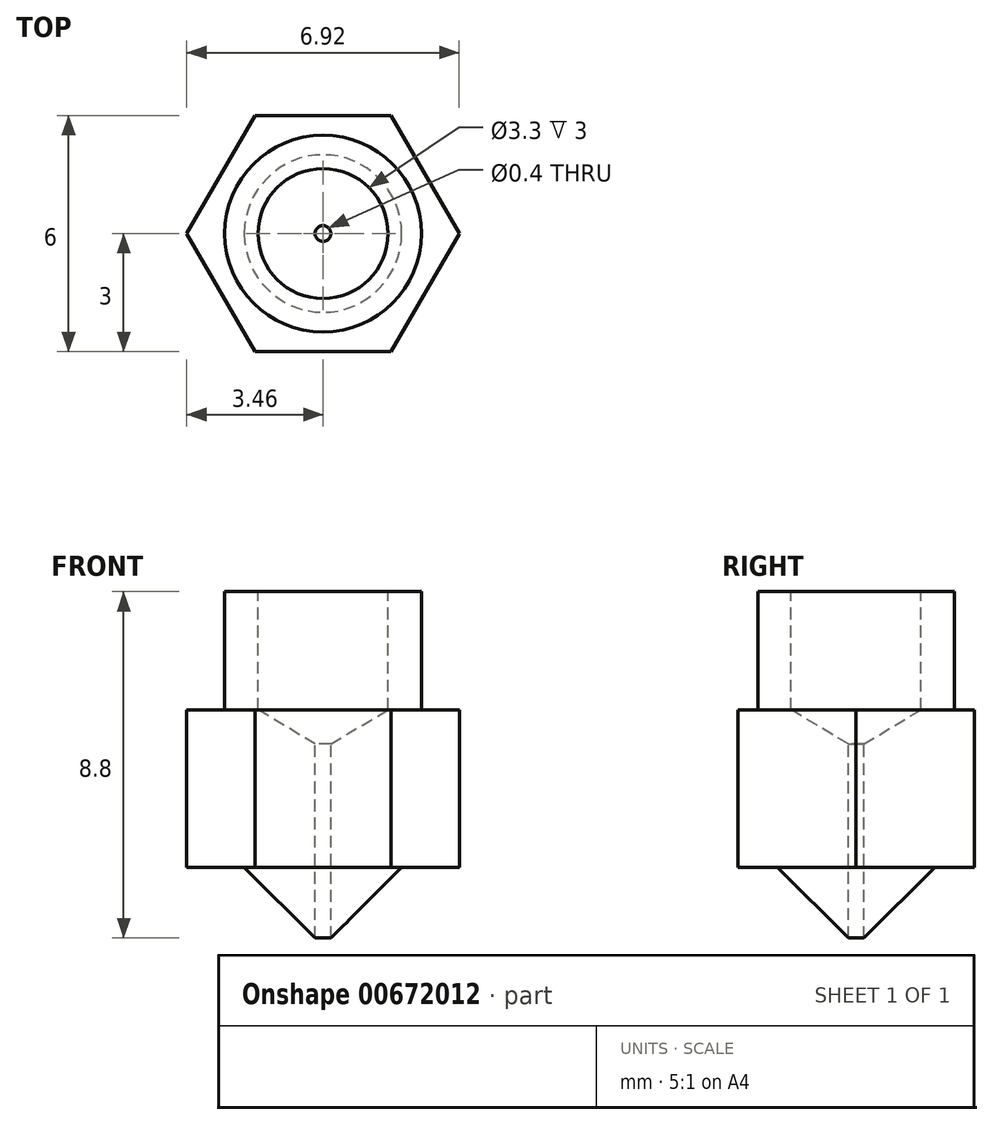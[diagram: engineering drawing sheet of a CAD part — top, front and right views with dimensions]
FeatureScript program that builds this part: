
annotation { "Feature Type Name" : "Feature", "Feature Type Description" : "" }
export const myFeature = defineFeature(function(context is Context, id is Id, definition is map)
    precondition{}
    {
        {
            var Q0;
            Q0=qCreatedBy(makeId("Front.planeOp"),FACE);
            var sketch = newSketch(context, id + "F0", { "sketchPlane" : qUnion([Q0])});
            skLineSegment(sketch, "E0", {"start": v(0, 0) * mm, "end": v(0, 3) * mm});
            skLineSegment(sketch, "E1", {"start": v(0, 3) * mm, "end": v(2.5, 3) * mm});
            skLineSegment(sketch, "E2", {"start": v(2.5, 3) * mm, "end": v(2.5, 0) * mm});
            skLineSegment(sketch, "E3", {"start": v(2.5, 0) * mm, "end": v(0, 0) * mm});
            skSolve(sketch);
        }
        {
            var Q0;
            Q0=makeQuery(id+"F0.imprint","IMPRINT",FACE,{"disambiguationData":[TD([[makeQuery(id+"F0.imprint","IMPRINT",EDGE,{"derivedFrom":sQuery(id+"F0.wireOp",EDGE,"E0")}),-1.0]])]});
            var Q1;
            Q1=sQuery(id+"F0.wireOp",EDGE,"E0");
            revolve(context, id + "F1", {"entities" : qUnion([Q0]), "axis" : qUnion([Q1]), "revolveType" : RevolveType.FULL});
        }
        {
            var Q0;
            Q0=makeQuery(id+"F1.opRevolve","SWEPT_FACE",FACE,{"disambiguationData":[OSD([sQuery(id+"F0.wireOp",EDGE,"E3")])]});
            var sketch = newSketch(context, id + "F2", { "sketchPlane" : qUnion([Q0])});
            skCircle(sketch, "E4.cCircle", {"center": v(0, 0) * mm, "radius": 3 * mm, "construction": true});
            skLineSegment(sketch, "E4.0", {"start": v(-1.73, 3) * mm, "end": v(1.73, 3) * mm});
            skLineSegment(sketch, "E4.1", {"start": v(1.73, 3) * mm, "end": v(3.46, 0) * mm});
            skLineSegment(sketch, "E4.2", {"start": v(3.46, 0) * mm, "end": v(1.73, -3) * mm});
            skLineSegment(sketch, "E4.3", {"start": v(1.73, -3) * mm, "end": v(-1.73, -3) * mm});
            skLineSegment(sketch, "E4.4", {"start": v(-1.73, -3) * mm, "end": v(-3.46, 0) * mm});
            skLineSegment(sketch, "E4.5", {"start": v(-3.46, 0) * mm, "end": v(-1.73, 3) * mm});
            skPoint(sketch, "E4.0.midPoint", {"position": v(0, 3) * mm});
            skSolve(sketch);
        }
        {
            var Q0;
            Q0=makeQuery(id+"F2.imprint","IMPRINT",FACE,{"disambiguationData":[TD([[makeQuery(id+"F2.imprint","IMPRINT",EDGE,{"derivedFrom":sQuery(id+"F2.wireOp",EDGE,"E4.0")}),-1.0]])]});
            var Q1;
            Q1=makeQuery(id+"F2.imprint","IMPRINT",FACE,{"disambiguationData":[TD([[makeQuery(id+"F2.imprint","IMPRINT",EDGE,{"derivedFrom":makeQuery(id+"F1.opRevolve","SWEPT_EDGE",EDGE,{"disambiguationData":[OSD([sQuery(id+"F0.wireOp",EDGE,"E2"),sQuery(id+"F0.wireOp",EDGE,"E3")])]})}),1.0]])]});
            extrude(context, id + "F3", {"entities" : qUnion([Q0, Q1]), "operationType" : NewBodyOperationType.ADD, "depth" : 4 * mm, "offsetDistance" : 25 * mm});
        }
        {
            var Q0;
            Q0=qCreatedBy(makeId("Front.planeOp"),FACE);
            var sketch = newSketch(context, id + "F4", { "sketchPlane" : qUnion([Q0])});
            skLineSegment(sketch, "E5", {"start": v(0, -4) * mm, "end": v(2, -4) * mm});
            skLineSegment(sketch, "E6", {"start": v(2, -4) * mm, "end": v(0, -6) * mm});
            skLineSegment(sketch, "E7", {"start": v(0, -6) * mm, "end": v(0, -4) * mm});
            skSolve(sketch);
        }
        {
            var Q0;
            Q0=makeQuery(id+"F4.imprint","IMPRINT",FACE,{"disambiguationData":[TD([[makeQuery(id+"F4.imprint","IMPRINT",EDGE,{"derivedFrom":sQuery(id+"F4.wireOp",EDGE,"E5")}),-1.0]])]});
            var Q1;
            Q1=sQuery(id+"F4.wireOp",EDGE,"E7");
            revolve(context, id + "F5", {"operationType" : NewBodyOperationType.ADD, "entities" : qUnion([Q0]), "axis" : qUnion([Q1]), "revolveType" : RevolveType.FULL});
        }
        {
            var Q0;
            Q0=makeQuery(id+"F1.opRevolve","SWEPT_FACE",FACE,{"disambiguationData":[OSD([sQuery(id+"F0.wireOp",EDGE,"E1")])]});
            var sketch = newSketch(context, id + "F6", { "sketchPlane" : qUnion([Q0])});
            skPoint(sketch, "E8", {"position": v(0, 0) * mm});
            skSolve(sketch);
        }
        {
            var Q0;
            Q0=sQuery(id+"F6.wireOp",VERTEX,"E8");
            var Q1;
            Q1=makeQuery(id+"F1.opRevolve","SWEPT_BODY",BODY,{"disambiguationData":[OSD([sQuery(id+"F0.wireOp",EDGE,"E0"),sQuery(id+"F0.wireOp",EDGE,"E1"),sQuery(id+"F0.wireOp",EDGE,"E2"),sQuery(id+"F0.wireOp",EDGE,"E3")])]});
            hole(context, id + "F7", {"style" : HoleStyle.SIMPLE, "endStyle" : HoleEndStyle.BLIND, "standardTappedOrClearance" : lookupTablePath({ "standard" : "ISO", "fit" : "Normal", "size" : "M3", "type" : "Clearance" }), "standardBlindInLast" : lookupTablePath({ "fit" : "Standard", "standard" : "ISO", "size" : "M3", "type" : "Clearance" }), "holeDiameter" : 3.3 * mm, "majorDiameter" : 3 * mm, "holeDepth" : 3 * mm, "isTappedThrough" : true, "tappedDepth" : 7.6 * mm, "tapClearance" : 3, "startFromSketch" : true, "locations" : qUnion([Q0]), "scope" : qUnion([Q1])});
        }
        {
            var Q0;
            Q0=makeQuery(id+"F1.opRevolve","SWEPT_FACE",FACE,{"disambiguationData":[OSD([sQuery(id+"F0.wireOp",EDGE,"E1")])]});
            var sketch = newSketch(context, id + "F8", { "sketchPlane" : qUnion([Q0])});
            skPoint(sketch, "E9", {"position": v(0, 0) * mm});
            skSolve(sketch);
        }
        {
            var Q0;
            Q0=sQuery(id+"F8.wireOp",VERTEX,"E9");
            var Q1;
            Q1=makeQuery(id+"F1.opRevolve","SWEPT_BODY",BODY,{"disambiguationData":[OSD([sQuery(id+"F0.wireOp",EDGE,"E0"),sQuery(id+"F0.wireOp",EDGE,"E1"),sQuery(id+"F0.wireOp",EDGE,"E2"),sQuery(id+"F0.wireOp",EDGE,"E3")])]});
            hole(context, id + "F9", {"style" : HoleStyle.SIMPLE, "endStyle" : HoleEndStyle.THROUGH, "holeDiameter" : .4 * mm, "majorDiameter" : 5 * mm, "isTappedThrough" : true, "tappedDepth" : 7.6 * mm, "tapClearance" : 3, "startFromSketch" : true, "locations" : qUnion([Q0]), "scope" : qUnion([Q1])});
        }
    });
